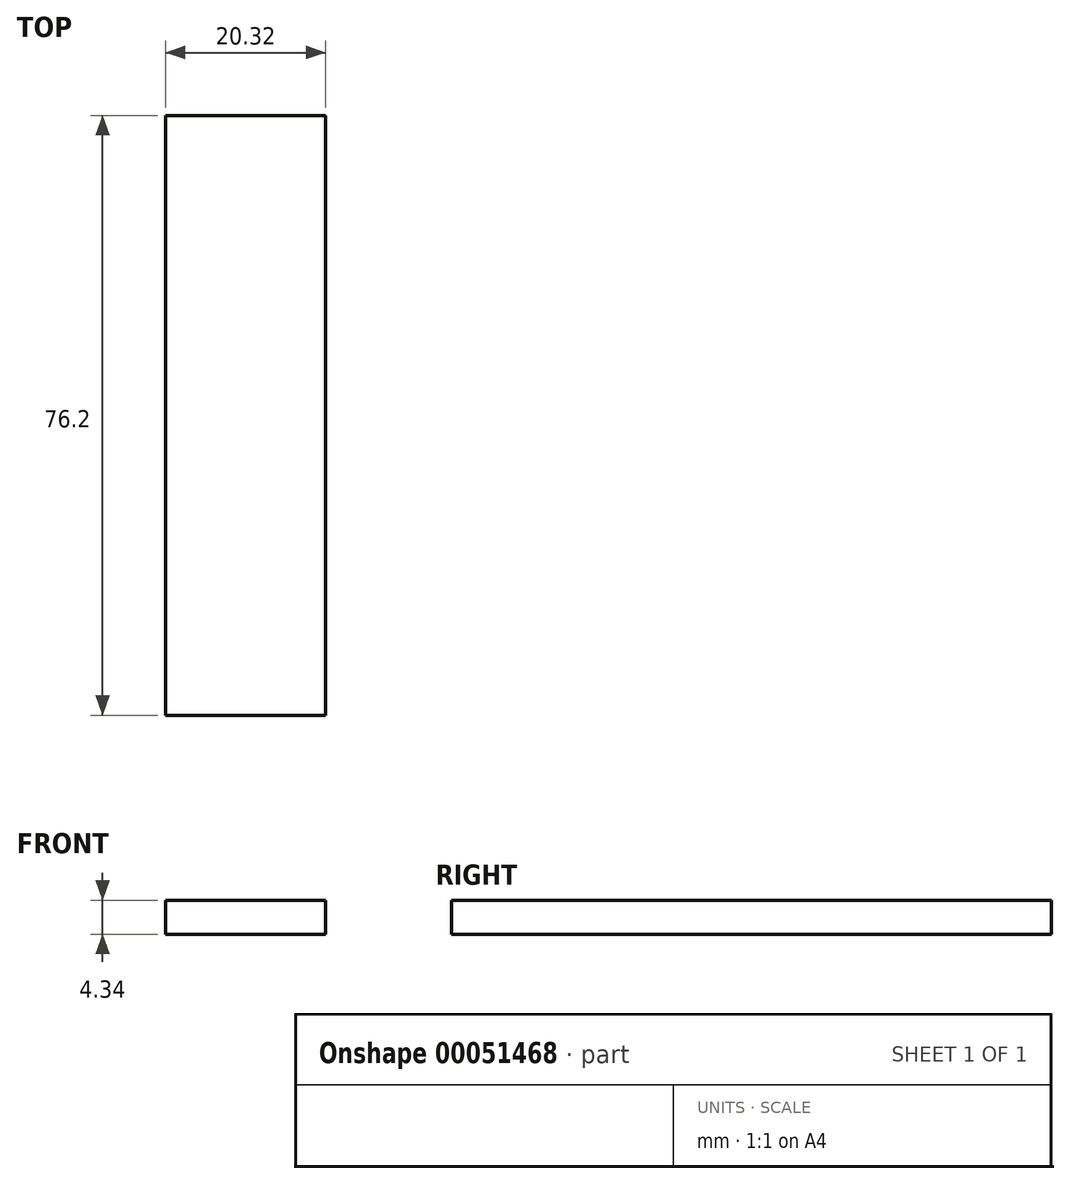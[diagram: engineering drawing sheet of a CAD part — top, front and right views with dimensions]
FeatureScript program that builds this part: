
annotation { "Feature Type Name" : "Feature", "Feature Type Description" : "" }
export const myFeature = defineFeature(function(context is Context, id is Id, definition is map)
    precondition{}
    {
        {
            var Q0;
            Q0=qCreatedBy(makeId("Top.planeOp"),FACE);
            var sketch = newSketch(context, id + "F0", { "sketchPlane" : qUnion([Q0])});
            skLineSegment(sketch, "E0.bottom", {"start": v(-12.7, 56.39) * mm, "end": v(7.62, 56.39) * mm});
            skLineSegment(sketch, "E0.top", {"start": v(-12.7, -19.81) * mm, "end": v(7.62, -19.81) * mm});
            skLineSegment(sketch, "E0.left", {"start": v(-12.7, 56.39) * mm, "end": v(-12.7, -19.81) * mm});
            skLineSegment(sketch, "E0.right", {"start": v(7.62, 56.39) * mm, "end": v(7.62, -19.81) * mm});
            skSolve(sketch);
        }
        {
            var Q0;
            Q0 = qSketchRegion(id + "F0", true);
            extrude(context, id + "F1", {"entities" : qUnion([Q0]), "oppositeDirection" : true, "depth" : 4.34 * mm});
        }
    });
